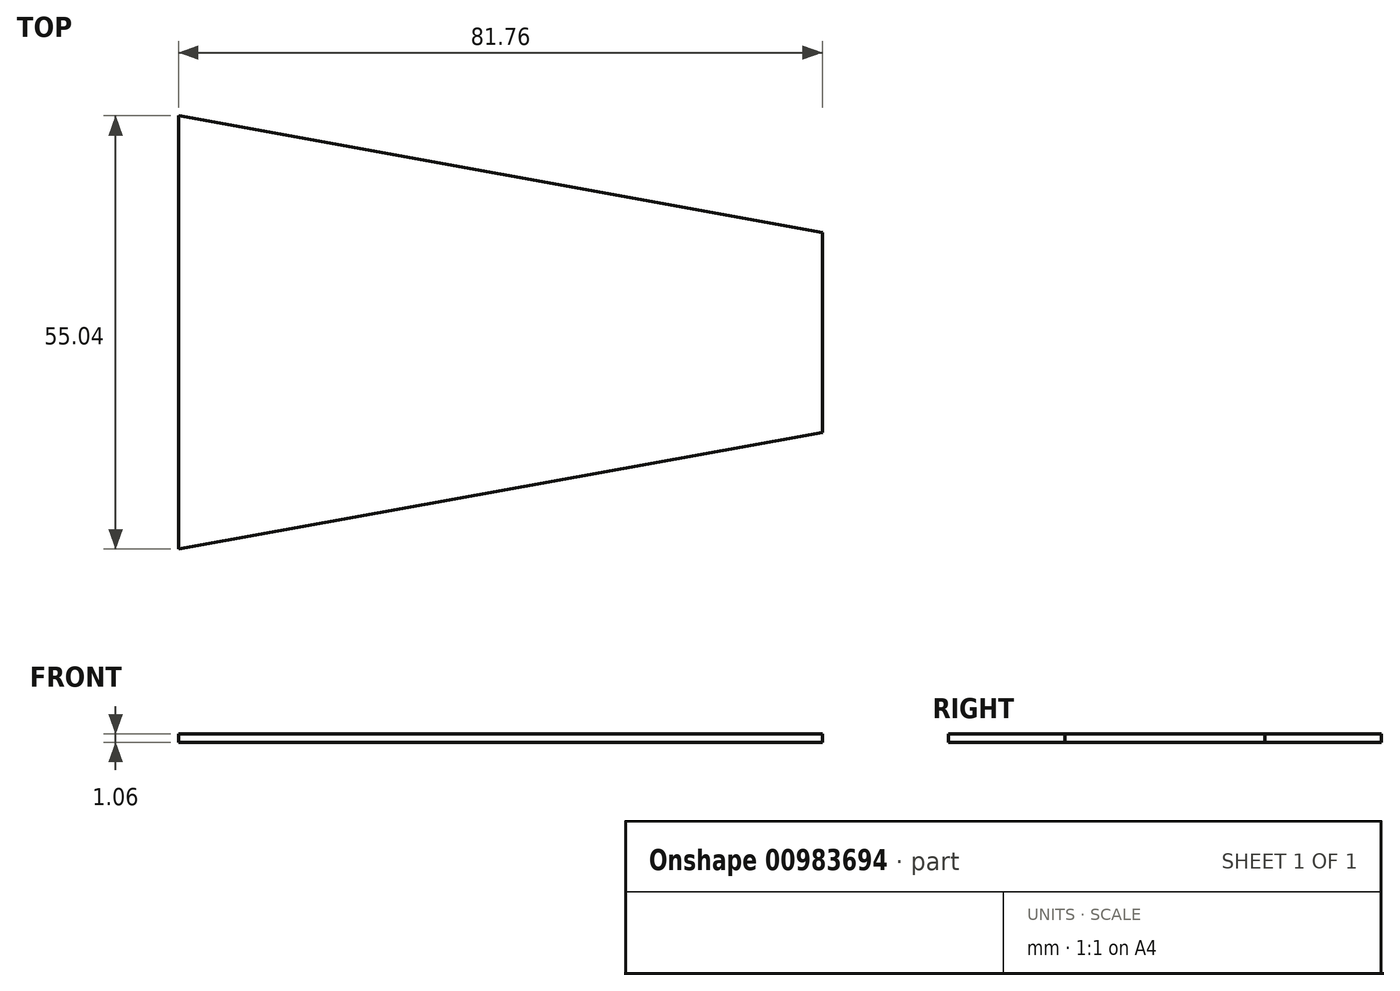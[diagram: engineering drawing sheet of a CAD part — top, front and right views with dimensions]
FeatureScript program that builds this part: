
annotation { "Feature Type Name" : "Feature", "Feature Type Description" : "" }
export const myFeature = defineFeature(function(context is Context, id is Id, definition is map)
    precondition{}
    {
        {
            var Q0;
            Q0=qCreatedBy(makeId("Top.planeOp"),FACE);
            var sketch = newSketch(context, id + "F0", { "sketchPlane" : qUnion([Q0])});
            skLineSegment(sketch, "E0.left", {"start": v(40.88, 12.7) * mm, "end": v(40.88, -12.7) * mm});
            skLineSegment(sketch, "E0.right", {"start": v(-40.88, 12.7) * mm, "end": v(-40.88, -12.7) * mm});
            skPoint(sketch, "E0.middle", {"position": v(0, 0) * mm});
            skLineSegment(sketch, "E1", {"start": v(-40.88, 12.7) * mm, "end": v(-40.88, 27.52) * mm});
            skLineSegment(sketch, "E2", {"start": v(-40.88, 27.52) * mm, "end": v(40.88, 12.7) * mm});
            skLineSegment(sketch, "E3", {"start": v(-40.88, -12.7) * mm, "end": v(-40.88, -27.52) * mm});
            skLineSegment(sketch, "E4", {"start": v(-40.88, -27.52) * mm, "end": v(40.88, -12.7) * mm});
            skLineSegment(sketch, "E5", {"start": v(-40.88, -12.7) * mm, "end": v(40.88, -12.7) * mm});
            skLineSegment(sketch, "E6", {"start": v(-40.88, 12.7) * mm, "end": v(40.88, 12.7) * mm});
            skSolve(sketch);
        }
        {
            var Q0;
            Q0 = qSketchRegion(id + "F0", true);
            extrude(context, id + "F1", {"entities" : qUnion([Q0]), "depth" : 1.06 * mm, "offsetDistance" : 25.4 * mm});
        }
    });
